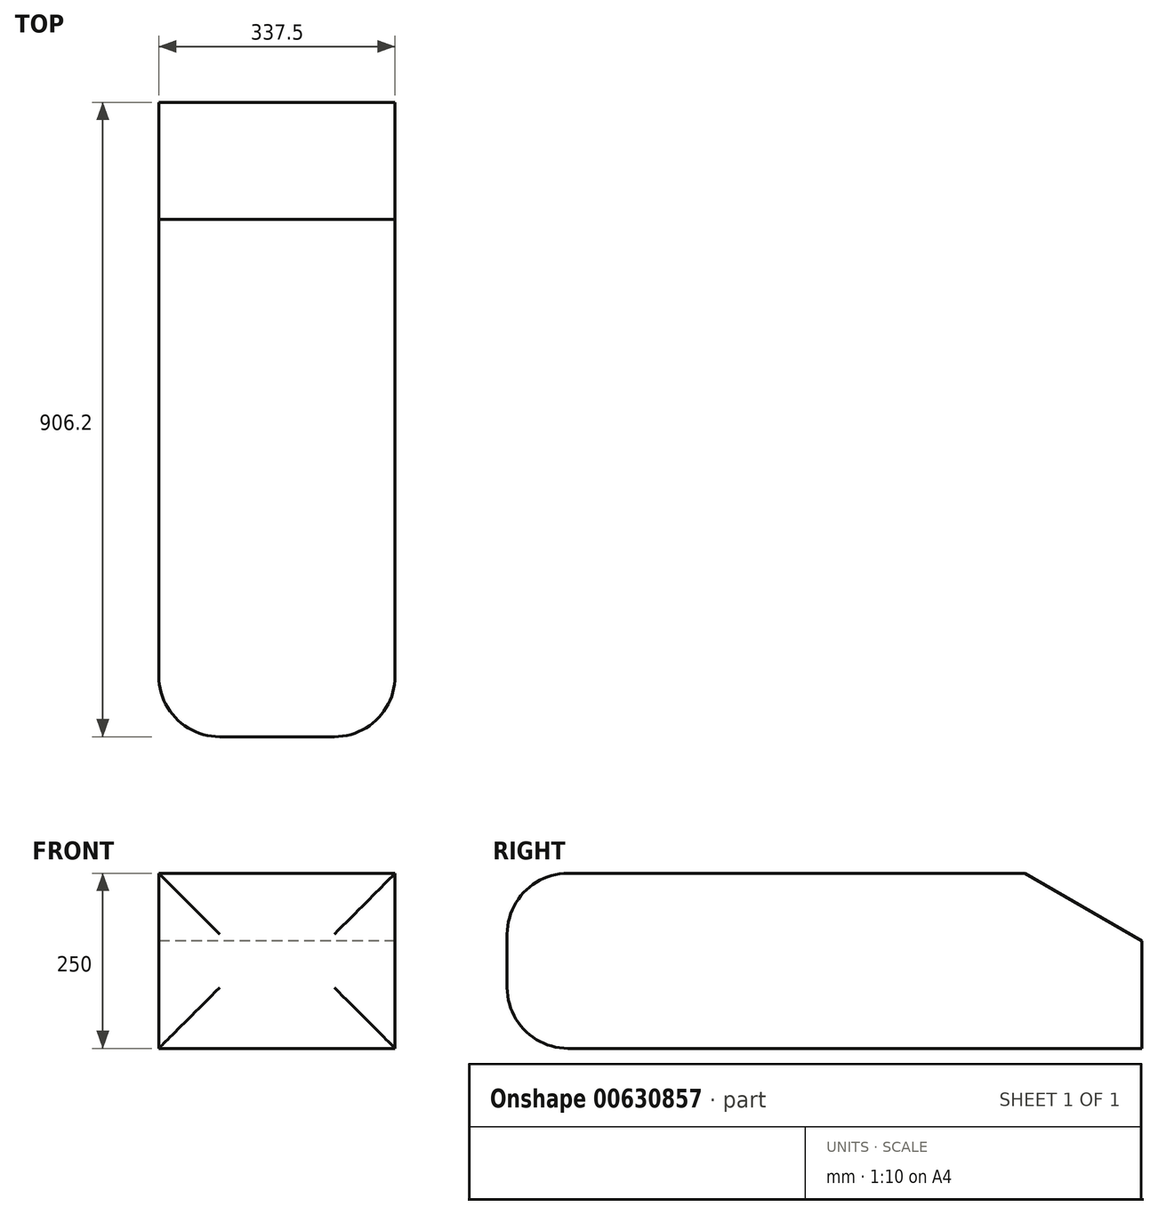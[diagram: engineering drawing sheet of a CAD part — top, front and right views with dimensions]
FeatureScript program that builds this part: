
annotation { "Feature Type Name" : "Feature", "Feature Type Description" : "" }
export const myFeature = defineFeature(function(context is Context, id is Id, definition is map)
    precondition{}
    {
        {
            assignVariable(context, id + "F0", {"name" : "Height", "anyValue" : 250});
        }
        {
            var Q0;
            Q0=qCreatedBy(makeId("Right.planeOp"),FACE);
            var sketch = newSketch(context, id + "F1", { "sketchPlane" : qUnion([Q0])});
            skLineSegment(sketch, "E0.bottom", {"start": v(0, 43.4) * mm, "end": v(906.2, 43.4) * mm});
            skLineSegment(sketch, "E0.top", {"start": v(0, 293.4) * mm, "end": v(739.32, 293.4) * mm});
            skLineSegment(sketch, "E0.left", {"start": v(0, 43.4) * mm, "end": v(0, 293.4) * mm});
            skLineSegment(sketch, "E0.right", {"start": v(906.2, 43.4) * mm, "end": v(906.2, 197.05) * mm});
            skLineSegment(sketch, "E1", {"start": v(739.32, 293.4) * mm, "end": v(906.2, 197.05) * mm});
            skSolve(sketch);
        }
        {
            var Q0;
            Q0 = qSketchRegion(id + "F1", true);
            extrude(context, id + "F2", {"entities" : qUnion([Q0]), "endBound" : BoundingType.SYMMETRIC, "depth" : (getVariable(context, 'Height')) * 1.35 * mm, "offsetDistance" : 25.4 * mm});
        }
        {
            var Q0;
            Q0=makeQuery(id+"F2.opExtrude","SWEPT_EDGE",EDGE,{"disambiguationData":[OSD([sQuery(id+"F1.wireOp",EDGE,"E0.top"),sQuery(id+"F1.wireOp",EDGE,"E0.left")])]});
            var Q1;
            Q1=makeQuery(id+"F2.opExtrude","CAP_EDGE",EDGE,{"disambiguationData":[OSD([sQuery(id+"F1.wireOp",EDGE,"E0.left")])],"isStart":false});
            var Q2;
            Q2=makeQuery(id+"F2.opExtrude","CAP_EDGE",EDGE,{"disambiguationData":[OSD([sQuery(id+"F1.wireOp",EDGE,"E0.left")])],"isStart":true});
            var Q3;
            Q3=makeQuery(id+"F2.opExtrude","SWEPT_EDGE",EDGE,{"disambiguationData":[OSD([sQuery(id+"F1.wireOp",EDGE,"E0.bottom"),sQuery(id+"F1.wireOp",EDGE,"E0.left")])]});
            fillet(context, id + "F3", {"entities" : qUnion([Q0, Q1, Q2, Q3]), "radius" : (getVariable(context, 'Height')) * 0.35 * mm, "tangentPropagation" : true, "allowEdgeOverflow" : false});
        }
    });
